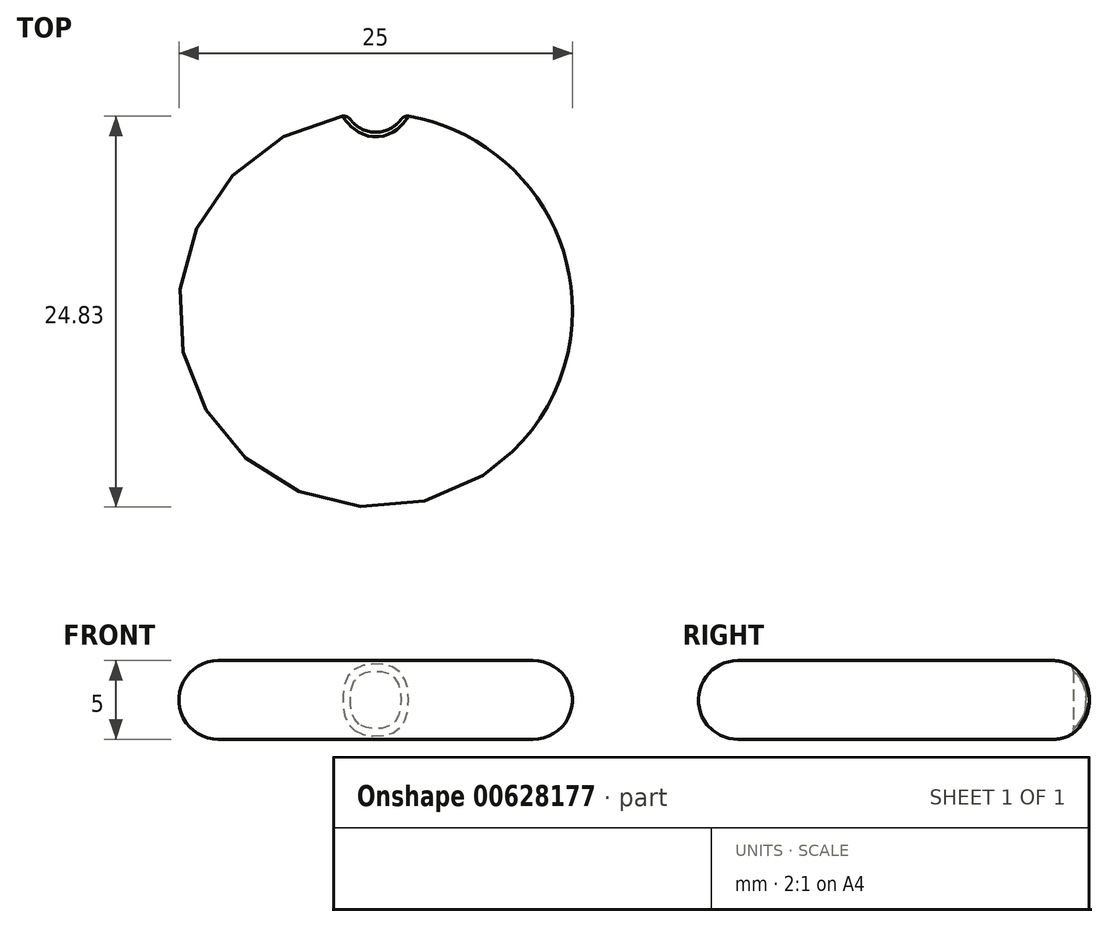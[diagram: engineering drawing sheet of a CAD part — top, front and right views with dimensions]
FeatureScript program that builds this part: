
annotation { "Feature Type Name" : "Feature", "Feature Type Description" : "" }
export const myFeature = defineFeature(function(context is Context, id is Id, definition is map)
    precondition{}
    {
        {
            var Q0;
            Q0=qCreatedBy(makeId("Front.planeOp"),FACE);
            var sketch = newSketch(context, id + "F0", { "sketchPlane" : qUnion([Q0])});
            skLineSegment(sketch, "E0", {"start": v(0, 0) * mm, "end": v(-10, 0) * mm});
            skArc(sketch, "E1", {"start": v(-10, 5) * mm, "mid": v(-12.5, 2.5) * mm, "end": v(-10, 0) * mm});
            skPoint(sketch, "E2.center.orphan", {"position": v(0, 48.23) * mm});
            skLineSegment(sketch, "E3", {"start": v(-10, 5) * mm, "end": v(0, 5) * mm});
            skLineSegment(sketch, "E4", {"start": v(0, 5) * mm, "end": v(0, 0) * mm});
            skSolve(sketch);
        }
        {
            var Q0;
            Q0=makeQuery(id+"F0.imprint","IMPRINT",FACE,{"disambiguationData":[TD([[makeQuery(id+"F0.imprint","IMPRINT",EDGE,{"derivedFrom":sQuery(id+"F0.wireOp",EDGE,"E0")}),-1.0]])]});
            var Q1;
            Q1=sQuery(id+"F0.wireOp",EDGE,"E4");
            revolve(context, id + "F1", {"entities" : qUnion([Q0]), "axis" : qUnion([Q1]), "revolveType" : RevolveType.FULL});
        }
        {
            var Q0;
            Q0=qCreatedBy(makeId("Top.planeOp"),FACE);
            var sketch = newSketch(context, id + "F2", { "sketchPlane" : qUnion([Q0])});
            skCircle(sketch, "E5", {"center": v(0, 13.31) * mm, "radius": 2 * mm});
            skSolve(sketch);
        }
        {
            var Q0;
            Q0=makeQuery(id+"F2.imprint","IMPRINT",FACE,{"disambiguationData":[TD([[makeQuery(id+"F2.imprint","IMPRINT",EDGE,{"derivedFrom":sQuery(id+"F2.wireOp",EDGE,"E5")}),1.0]])]});
            extrude(context, id + "F3", {"entities" : qUnion([Q0]), "operationType" : NewBodyOperationType.REMOVE, "depth" : 23.5 * mm, "offsetDistance" : 25 * mm});
        }
        {
            var Q0;
            Q0=makeQuery(id+"F3.boolean.opBoolean","INTERSECT",EDGE,{"derivedFrom":[makeQuery(id+"F1.opRevolve","SWEPT_FACE",FACE,{"disambiguationData":[OSD([sQuery(id+"F0.wireOp",EDGE,"E1")])]}),makeQuery(id+"F3.opExtrude","SWEPT_FACE",FACE,{"disambiguationData":[OSD([sQuery(id+"F2.wireOp",EDGE,"E5")])]})]});
            fillet(context, id + "F4", {"entities" : qUnion([Q0]), "radius" : 0.5 * mm, "tangentPropagation" : true, "allowEdgeOverflow" : false});
        }
    });
